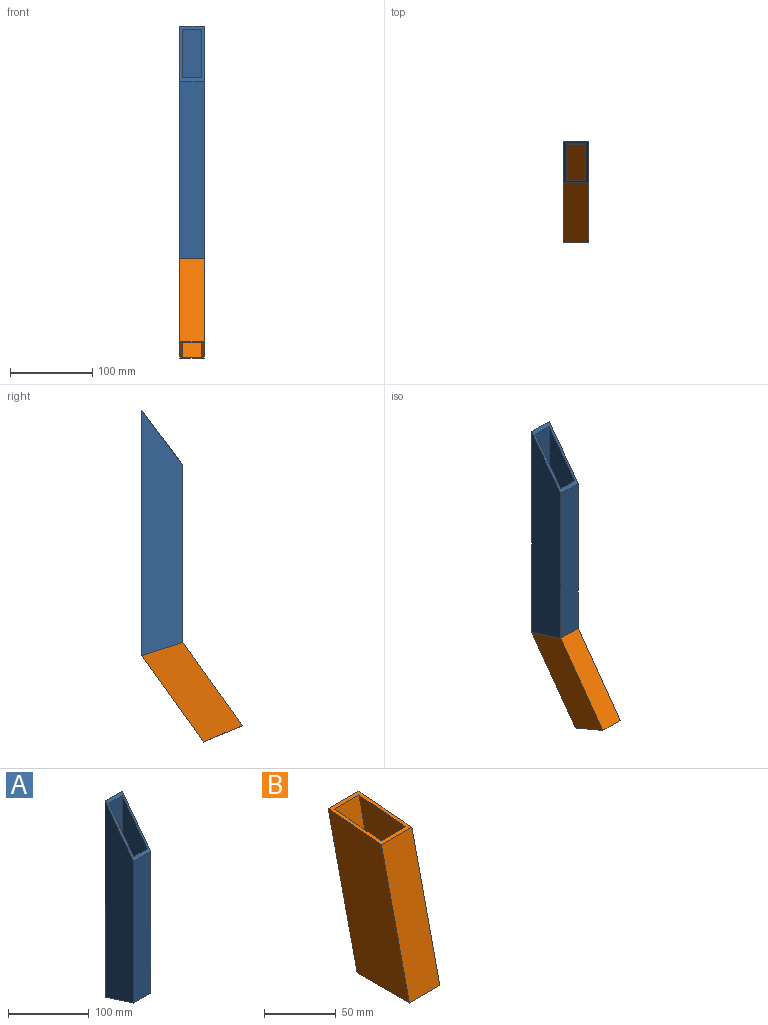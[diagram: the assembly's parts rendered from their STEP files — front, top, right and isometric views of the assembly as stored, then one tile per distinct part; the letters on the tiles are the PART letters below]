
ASSEMBLY  parts=2 mates=1
PART A: 10 faces, bbox 30x50x298 mm
  f0: plane 298x50mm, normal (1,0,0), area 12827.8mm2, adj f1,f7,f8,f9
  f1: plane 215.11x30mm, normal (0,-1,0), area 6453.3mm2, adj f0,f2,f7,f9
  f2: plane 298x50mm, normal (-1,0,0), area 12827.8mm2, adj f1,f7,f8,f9
  f3: plane 293.03x24mm, normal (0,-1,0), area 7032.6mm2, adj f4,f6,f7,f9
  f4: plane 293.03x44mm, normal (1,0,0), area 11288.4mm2, adj f3,f5,f7,f9
  f5: plane 220.08x24mm, normal (0,1,0), area 5282mm2, adj f4,f6,f7,f9
  f6: plane 293.03x44mm, normal (-1,0,0), area 11288.4mm2, adj f3,f5,f7,f9
  f7: plane 50x30mm, normal (0,-0.31,-0.95), area 466.3mm2, adj f0,f1,f2,f3,f4,f5,f6,f8
  f8: plane 298x30mm, normal (0,1,0), area 8940mm2, adj f0,f2,f7,f9
  f9: plane 66.84x50mm, normal (0,-0.8,0.6), area 741.2mm2, adj f0,f1,f2,f3,f4,f5,f6,f8
PART B: 10 faces, bbox 30x79.8x125.4 mm
  f0: plane 120.87x30mm, normal (0,-0.98,0.22), area 3718.4mm2, adj f1,f2,f8,f9
  f1: plane 125.44x79.77mm, normal (1,0,0), area 6314.7mm2, adj f0,f7,f8,f9
  f2: plane 125.44x79.77mm, normal (-1,0,0), area 6314.7mm2, adj f0,f7,f8,f9
  f3: plane 125.17x73.56mm, normal (1,0,0), area 5556.9mm2, adj f4,f6,f8,f9
  f4: plane 121.14x27.52mm, normal (0,0.98,-0.22), area 2981.5mm2, adj f3,f5,f8,f9
  f5: plane 125.17x73.56mm, normal (-1,0,0), area 5556.9mm2, adj f4,f6,f8,f9
  f6: plane 125.17x28.44mm, normal (0,-0.98,0.22), area 3080.6mm2, adj f3,f5,f8,f9
  f7: plane 125.44x30mm, normal (0,0.98,-0.22), area 3859.2mm2, adj f1,f2,f8,f9
  f8: plane 51.27x30mm, normal (0,0,-1), area 455.3mm2, adj f0,f1,f2,f3,f4,f5,f6,f7
  f9: plane 52.31x30mm, normal (0,-0.09,1), area 466.3mm2, adj f0,f1,f2,f3,f4,f5,f6,f7
PLACE A t=(-158.81,58.76,-276.41)mm
PLACE B rot(axis=(-1,0,0),22.8deg) t=(-158.81,-13.39,-361.14)mm
MATE fastened B.f9 <-> A.f7  axis (0,0.31,0.95) through (-158.81,58.76,-260.36)mm
